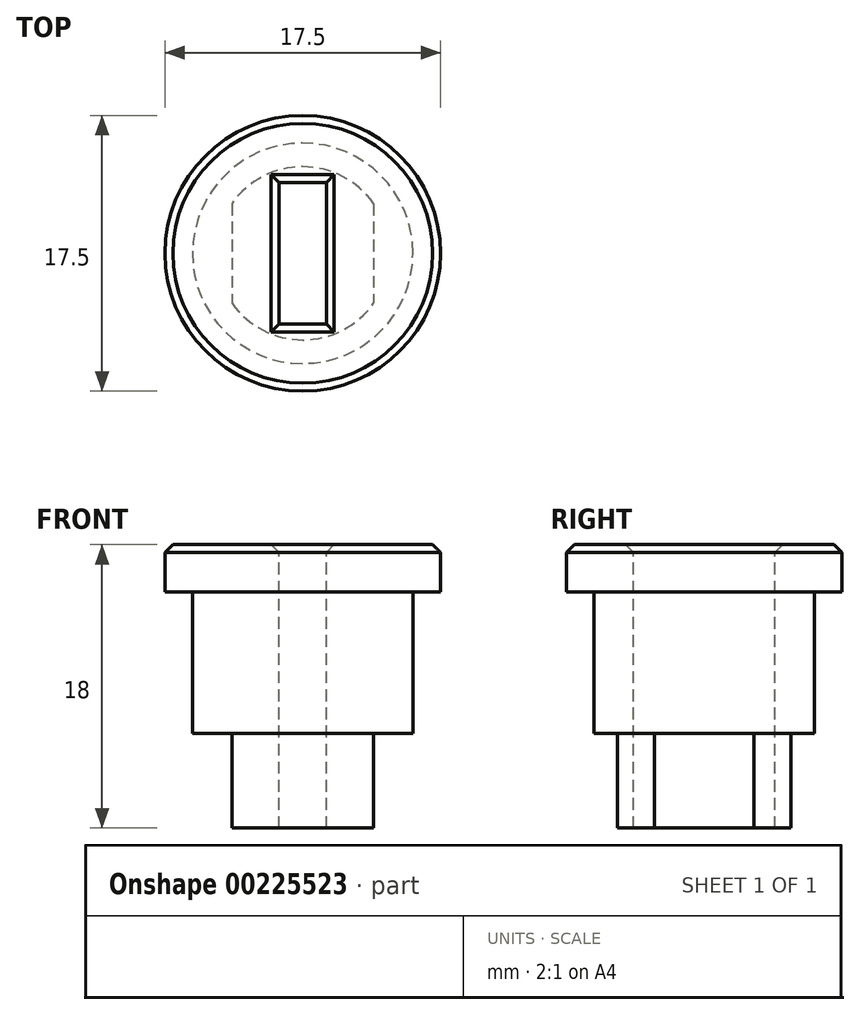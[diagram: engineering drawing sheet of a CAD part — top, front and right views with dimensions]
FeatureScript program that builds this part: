
annotation { "Feature Type Name" : "Feature", "Feature Type Description" : "" }
export const myFeature = defineFeature(function(context is Context, id is Id, definition is map)
    precondition{}
    {
        {
            var Q0;
            Q0=qCreatedBy(makeId("Top.planeOp"),FACE);
            var sketch = newSketch(context, id + "F0", { "sketchPlane" : qUnion([Q0])});
            skCircle(sketch, "E0", {"center": v(0, 0) * mm, "radius": 8.75 * mm});
            skSolve(sketch);
        }
        {
            var Q0;
            Q0=qCreatedBy(makeId("Top.planeOp"),FACE);
            var sketch = newSketch(context, id + "F1", { "sketchPlane" : qUnion([Q0])});
            skCircle(sketch, "E1", {"center": v(0, 0) * mm, "radius": 7 * mm});
            skSolve(sketch);
        }
        {
            var Q0;
            Q0=qCreatedBy(makeId("Top.planeOp"),FACE);
            var sketch = newSketch(context, id + "F2", { "sketchPlane" : qUnion([Q0])});
            skArc(sketch, "E2", {"start": v(4.5, 3.16) * mm, "mid": v(0, 5.5) * mm, "end": v(-4.5, 3.16) * mm});
            skLineSegment(sketch, "E3", {"start": v(4.5, 3.16) * mm, "end": v(4.5, -3.16) * mm});
            skLineSegment(sketch, "E4", {"start": v(-4.5, 3.16) * mm, "end": v(-4.5, -3.16) * mm});
            skArc(sketch, "E5.trimOffspring", {"start": v(-4.5, -3.16) * mm, "mid": v(0, -5.5) * mm, "end": v(4.5, -3.16) * mm});
            skSolve(sketch);
        }
        {
            var Q0;
            Q0 = qSketchRegion(id + "F0", true);
            extrude(context, id + "F3", {"entities" : qUnion([Q0]), "depth" : 3 * mm});
        }
        {
            var Q0;
            Q0 = qSketchRegion(id + "F1", true);
            extrude(context, id + "F4", {"entities" : qUnion([Q0]), "operationType" : NewBodyOperationType.ADD, "oppositeDirection" : true, "depth" : 9 * mm});
        }
        {
            var Q0;
            Q0 = qSketchRegion(id + "F2", true);
            extrude(context, id + "F5", {"entities" : qUnion([Q0]), "operationType" : NewBodyOperationType.ADD, "oppositeDirection" : true, "depth" : 15 * mm});
        }
        {
            var Q0;
            Q0=qCreatedBy(makeId("Top.planeOp"),FACE);
            var sketch = newSketch(context, id + "F6", { "sketchPlane" : qUnion([Q0])});
            skLineSegment(sketch, "E6.bottom", {"start": v(-1.5, -4.5) * mm, "end": v(1.5, -4.5) * mm});
            skLineSegment(sketch, "E6.top", {"start": v(-1.5, 4.5) * mm, "end": v(1.5, 4.5) * mm});
            skLineSegment(sketch, "E6.left", {"start": v(-1.5, -4.5) * mm, "end": v(-1.5, 4.5) * mm});
            skLineSegment(sketch, "E6.right", {"start": v(1.5, -4.5) * mm, "end": v(1.5, 4.5) * mm});
            skSolve(sketch);
        }
        {
            var Q0;
            Q0 = qSketchRegion(id + "F6", true);
            extrude(context, id + "F7", {"entities" : qUnion([Q0]), "operationType" : NewBodyOperationType.REMOVE, "endBound" : BoundingType.SYMMETRIC, "oppositeDirection" : true, "depth" : 40 * mm});
        }
        {
            var Q0;
            Q0=makeQuery(id+"F3.opExtrude","CAP_FACE",FACE,{"disambiguationData":[OSD([sQuery(id+"F0.wireOp",EDGE,"E0")])],"isStart":false});
            chamfer(context, id + "F8", {"entities" : qUnion([Q0]), "width" : .5 * mm, "tangentPropagation" : true});
        }
    });
